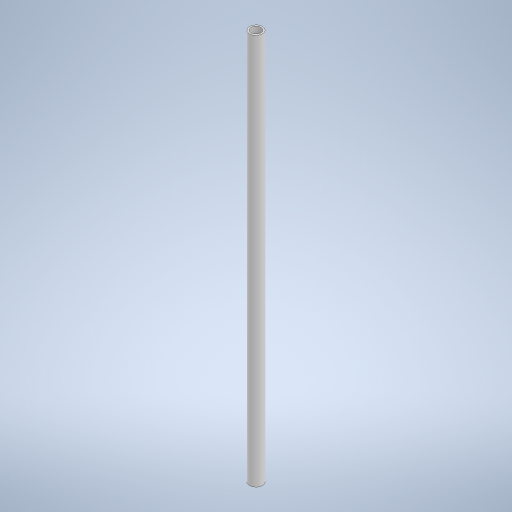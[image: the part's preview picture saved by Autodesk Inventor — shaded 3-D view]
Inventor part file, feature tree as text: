
AUTODESK INVENTOR PART (.ipt)
format: ipt  version: 2024.3 (Build 283343000, 343)  size: 232,960 bytes
history: native  units: in
note: dims shown in document units (in); Inventor stores cm internally (conversion verified against a paired STEP export)
features: extrude x1, sketch x1
ambient origin geometry x8: Origin, YZ Plane, XZ Plane, XY Plane, X Axis, Y Axis, Z Axis, Center Point
bodies: Solid1 (feature_tree)
feature tree (2):
  extrude  "Extrusion1"  Depth=4.7244in
  sketch  "Sketch1"  dims[d0=0.1181in d1=0.1575in d2=4.7244in d3=0.0in]
